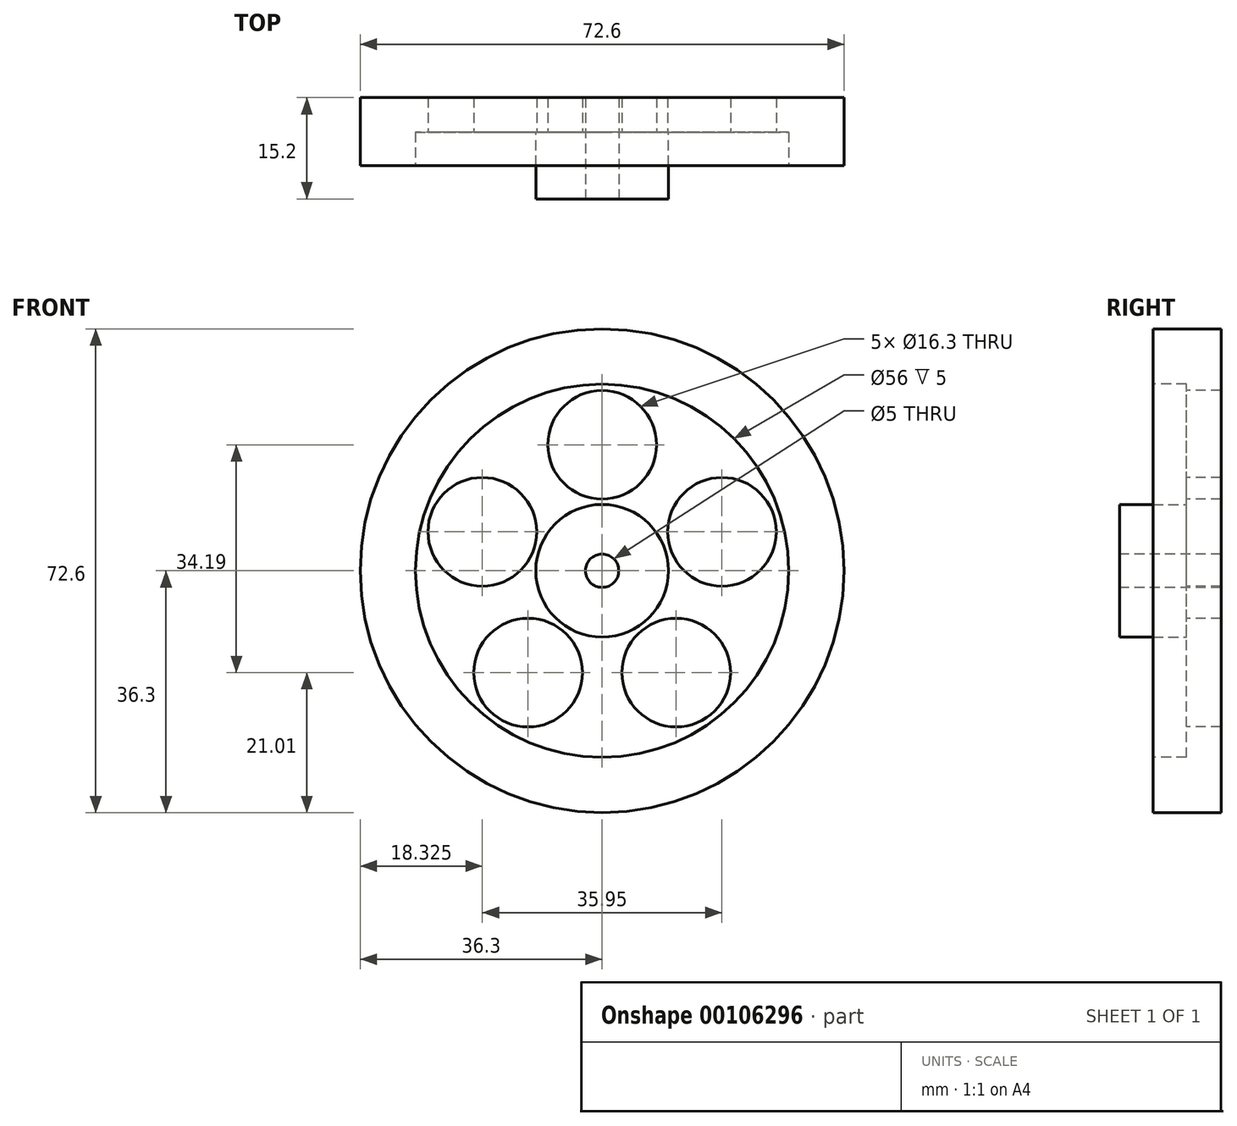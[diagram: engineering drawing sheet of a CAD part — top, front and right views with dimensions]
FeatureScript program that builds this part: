
annotation { "Feature Type Name" : "Feature", "Feature Type Description" : "" }
export const myFeature = defineFeature(function(context is Context, id is Id, definition is map)
    precondition{}
    {
        {
            var Q0;
            Q0=qCreatedBy(makeId("Front.planeOp"),FACE);
            var sketch = newSketch(context, id + "F0", { "sketchPlane" : qUnion([Q0])});
            skCircle(sketch, "E0", {"center": v(0, 0) * mm, "radius": 36.3 * mm});
            skSolve(sketch);
        }
        {
            var Q0;
            Q0=qSketchRegion(id+"F0",true);
            extrude(context, id + "F1", {"entities" : qUnion([Q0]), "depth" : 10.2 * mm});
        }
        {
            var Q0;
            Q0=makeQuery(id+"F1.opExtrude","CAP_FACE",FACE,{"disambiguationData":[OSD([sQuery(id+"F0.wireOp",EDGE,"E0")])],"isStart":false});
            var sketch = newSketch(context, id + "F2", { "sketchPlane" : qUnion([Q0])});
            skCircle(sketch, "E1", {"center": v(0, 0) * mm, "radius": 28 * mm});
            skSolve(sketch);
        }
        {
            var Q0;
            Q0=qSketchRegion(id+"F2",true);
            extrude(context, id + "F3", {"entities" : qUnion([Q0]), "operationType" : NewBodyOperationType.REMOVE, "oppositeDirection" : true, "depth" : 5 * mm});
        }
        {
            var Q0;
            Q0=makeQuery(id+"F3.boolean.opBoolean","COPY",FACE,{"derivedFrom":makeQuery(id+"F3.opExtrude","CAP_FACE",FACE,{"disambiguationData":[OSD([sQuery(id+"F2.wireOp",EDGE,"E1")])],"isStart":false})});
            var sketch = newSketch(context, id + "F4", { "sketchPlane" : qUnion([Q0])});
            skCircle(sketch, "E2", {"center": v(0, 0) * mm, "radius": 9.95 * mm});
            skSolve(sketch);
        }
        {
            var Q0;
            Q0=qSketchRegion(id+"F4",true);
            extrude(context, id + "F5", {"entities" : qUnion([Q0]), "operationType" : NewBodyOperationType.ADD, "depth" : 10 * mm});
        }
        {
            var Q0;
            Q0=makeQuery(id+"F5.opExtrude","CAP_FACE",FACE,{"disambiguationData":[OSD([sQuery(id+"F4.wireOp",EDGE,"E2")])],"isStart":false});
            var sketch = newSketch(context, id + "F6", { "sketchPlane" : qUnion([Q0])});
            skCircle(sketch, "E3", {"center": v(0, 0) * mm, "radius": 2.5 * mm});
            skSolve(sketch);
        }
        {
            var Q0;
            Q0=qSketchRegion(id+"F6",true);
            extrude(context, id + "F7", {"entities" : qUnion([Q0]), "operationType" : NewBodyOperationType.REMOVE, "endBound" : BoundingType.THROUGH_ALL, "oppositeDirection" : true, "depth" : 25 * mm});
        }
        {
            var Q0;
            Q0=makeQuery(id+"F3.boolean.opBoolean","COPY",FACE,{"derivedFrom":makeQuery(id+"F3.opExtrude","CAP_FACE",FACE,{"disambiguationData":[OSD([sQuery(id+"F2.wireOp",EDGE,"E1")])],"isStart":false})});
            var sketch = newSketch(context, id + "F8", { "sketchPlane" : qUnion([Q0])});
            skCircle(sketch, "E4", {"center": v(0, 18.9) * mm, "radius": 8.15 * mm});
            skCircle(sketch, "E5.1.0", {"center": v(-17.97, 5.84) * mm, "radius": 8.15 * mm});
            skCircle(sketch, "E5.2.0", {"center": v(-11.1, -15.3) * mm, "radius": 8.15 * mm});
            skCircle(sketch, "E5.3.0", {"center": v(11.1, -15.3) * mm, "radius": 8.15 * mm});
            skCircle(sketch, "E5.4.0", {"center": v(17.97, 5.84) * mm, "radius": 8.15 * mm});
            skPoint(sketch, "E5.center", {"position": v(0, 0) * mm});
            skSolve(sketch);
        }
        {
            var Q0;
            Q0=qSketchRegion(id+"F8",true);
            extrude(context, id + "F9", {"entities" : qUnion([Q0]), "operationType" : NewBodyOperationType.REMOVE, "endBound" : BoundingType.THROUGH_ALL, "oppositeDirection" : true, "depth" : 25 * mm});
        }
    });
